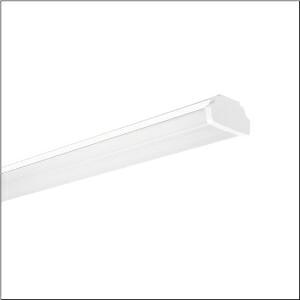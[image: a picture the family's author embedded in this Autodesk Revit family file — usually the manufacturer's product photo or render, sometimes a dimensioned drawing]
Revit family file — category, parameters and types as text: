
# Revit family: modario_r__31_gen_2_53bm8127v68xc2_4e77
name_source: partatom
category: Lighting Fixtures
units: mm (PartAtom-declared; Revit-internal decimal feet)

## family parameters
Cut with Voids When Loaded = No
Host = Face
Light Source = No
Part Type = Normal
Room Calculation Point = No
Round Connector Dimension = Use Diameter
Shared = No

## types (1)
- Modario® 31 Gen.2 (1 x LED, 8340 lm, 47.9 W, 6500K)
    Apparent Load = 48 VA
    CIE Flux Codes = 47 80 95 93 100
    Color Rendering = 80
    Color Temperature = 6500K
    Default Elevation = 1800 mm
    Description = Modario® 31 Gen.2, luminaire insert, of sheet steel, coil coated, white, length: 1.495mm, width: 81mm, height: 82mm, 5x system unit, system units: 299mm, LED rated luminous flux: 8.340lm, light colour: 865, control gear: ON/OFF, control gear: ECG, with plug, 3-pole, with phase selection, mains connection: 220..240V, AC, 50/60Hz, rated input power: 48W, through-wiring accessed according to module size, primary optical cover: cover, of PMMA, light emission: direct distribution, primary light characteristic: symmetric, protection rating (complete): IP20, protection rating (LED compartment): IP50, insulation class (complete): insulation class I (protective earthing), certification: CE, ENEC, VDE, UKCA, impact resistance: IK03, permissible ambient temperature for indoor applications: -35..+45°C, corresponds to IFS (International Featured Standards) requirements for safety and quality in the food industry, reducing of maximum allowable ambient temperature of 5°C with ceiling mounting, IP40 when using the optional accessory 5TP9018, packaging unit: 1 piece
    Height = 92 mm
    Lamp = 1 x LED
    Lamp Light Flux = 8340 lm
    Lamp Power = 47.9 W
    Lamp count = 1
    Length = 1495 mm
    Luminous efficacy = 174 lm/W
    Manufacturer = Siteco
    ModVariant = No
    Model = 53BM8127V68XC2
    Mounting Place = Ceiling
    Mounting Type = Pendant
    Number of Poles = 1
    OnlyDefault = Yes
    Power Factor = 1
    Product Name = Modario® 31 Gen.2
    Product group = luminaire insert
    ProductGroupID = 901
    Protection Class = Protection class I
    Protection Degree = IP 20
    RLX_Detail_Level = 1
    RLX_Emergency_Light_Flux = 0 lm
    RLX_Emergency_Type = 0
    RLX_Emergency_Type_DB = No
    RlxData = <blob elided: 38761 chars, md5=ab3e9ec8>
    Socket = socket
    Standby Power = 0 W
    System Light Flux = 8340 lm
    System Power = 48 W
    Type Comments = Product without accessories
    Type Image = l_1319597.jpg
    URL = http://relux.com
    VarID = ---
    Voltage = 0 V
    Weight = 0.00 kg
    Width = 81 mm

## geometry (parser evidence)
native form markers: Blend x4, Sweep x12
no freeform markers — native parametric forms only
